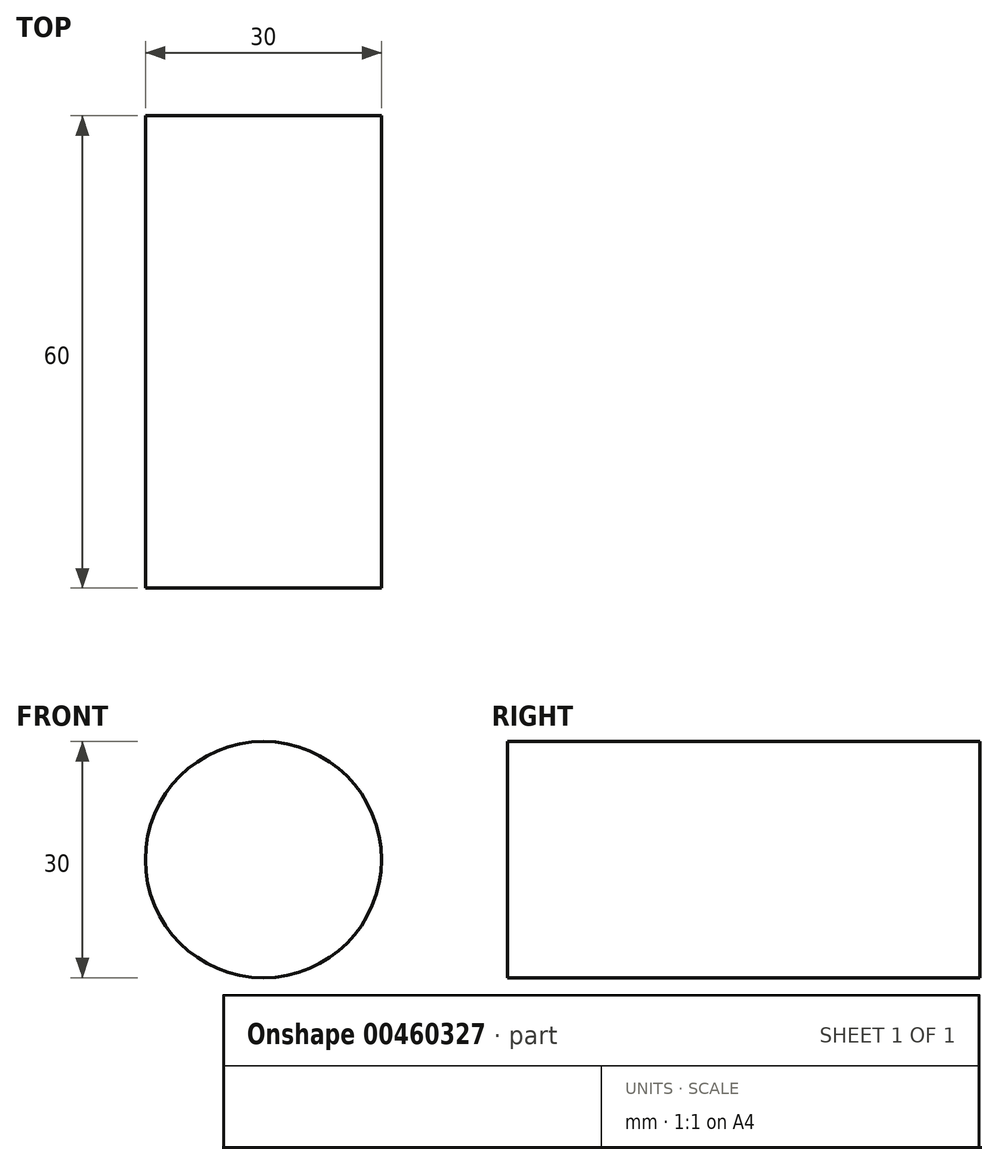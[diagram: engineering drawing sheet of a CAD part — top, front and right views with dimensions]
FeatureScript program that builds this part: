
annotation { "Feature Type Name" : "Feature", "Feature Type Description" : "" }
export const myFeature = defineFeature(function(context is Context, id is Id, definition is map)
    precondition{}
    {
        {
            var Q0;
            Q0=qCreatedBy(makeId("Front.planeOp"),FACE);
            var sketch = newSketch(context, id + "F0", { "sketchPlane" : qUnion([Q0])});
            skCircle(sketch, "E0", {"center": v(0, 0) * mm, "radius": 15 * mm});
            skSolve(sketch);
        }
        {
            var Q0;
            Q0 = qSketchRegion(id + "F0", true);
            extrude(context, id + "F1", {"entities" : qUnion([Q0]), "depth" : 60 * mm});
        }
    });
